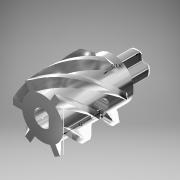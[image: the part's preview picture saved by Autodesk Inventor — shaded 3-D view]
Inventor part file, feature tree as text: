
AUTODESK INVENTOR PART (.ipt)
format: ipt  version: 2016 (Build 200138000, 138)  size: 539,648 bytes
history: native  units: mm
features: sketch x10, extrude x4, other x3, hole x3, plane x2, fillet x2, revolve x1, loft x1, sweep x1, chamfer x1, pattern_circular x1, projected_geometry x1
ambient origin geometry x8: Origin, YZ Plane, XZ Plane, XY Plane, X Axis, Y Axis, Z Axis, Center Point
bodies: Solid1 (feature_tree)
feature tree (30):
  extrude  "Extrusion1"  Depth=20.0mm TaperAngle=0.0deg
  other  "Work Axis1"
  plane  "Work Plane1"
  extrude  "Extrusion2"  Depth=3.0mm TaperAngle=0.0deg
  extrude  "Extrusion3"  Depth=2.7mm
  revolve  "Revolution1"  [1 undecoded]
  fillet  "Fillet6"  Radius=8.6mm
  fillet  "Fillet2"  Radius=0.4mm
  plane  "Work Plane2"
  sketch  "Sketch7"  dims[d38=1.5mm d43=12.0mm]
  loft  "Loft2"
  hole  "Hole1"  [1 undecoded]
  extrude  "Extrusion5"  TaperAngle=0.0deg  [1 undecoded]
  sweep  "Sweep1"
  chamfer  "Chamfer1"  Distance=10.0mm
  pattern_circular  "Circular Pattern1"  [2 undecoded]
  sketch  "Sketch2"  dims[d90=10.0mm d91=10.0mm d5=5.4mm d6=6.0mm d7=4.0mm d8=2.0mm d9=90.0deg d10=20.0mm d11=20.594885mm]
  hole  "Hole2"  [1 undecoded]
  hole  "Hole3"  [1 undecoded]
  sketch  "Sketch14"  dims[d52=1.4mm d57=23.5mm d70=10.0mm d71=0.0mm d75=2.02mm d76=2.0mm d77=3.0mm d78=60.0mm d79=20.0mm d80=13.5mm d81=0.0mm d82=0.0mm d83=0.0mm d84=60.0mm d85=360.0deg d87=2.0mm d88=12.0mm d89=45.0deg d92=6.0mm d93=6.0mm d94=4.0mm d95=2.0mm d96=90.0deg d97=8.0mm d98=20.594885mm d55=1.0mm d56=1.0mm]
  sketch  "Sketch1"  dims[d0=13.5mm d1=20.0mm d2=0.0mm]
  sketch  "Sketch3"  dims[d13=6.75mm d14=5.2mm d15=6.0mm d16=6.0mm d17=2.0mm d18=90.0deg d19=13.5mm d20=20.594885mm d23=3.0mm d24=0.0mm]
  sketch  "Sketch4"  dims[d25=2.7mm d26=2.7mm]
  sketch  "Sketch6"  dims[d27=9.0mm d28=9.0mm d29=8.6mm d30=0.0mm d32=0.4mm]
  projected_geometry  "Projected Loop2"
  other  "Edges2"
  sketch  "Sketch11"  dims[d44=90.0deg d47=0.6mm]
  sketch  "Sketch12"  dims[d48=0.0mm d49=90.0deg d50=0.0mm d51=90.0deg]
  sketch  "3D Sketch1"
  other  "Helical Curve1"
note: 7 required parameter values undecoded (feature->parameter linkage not recoverable at this tier; creation-order binding heuristic only, values carry confidence <= 0.55)